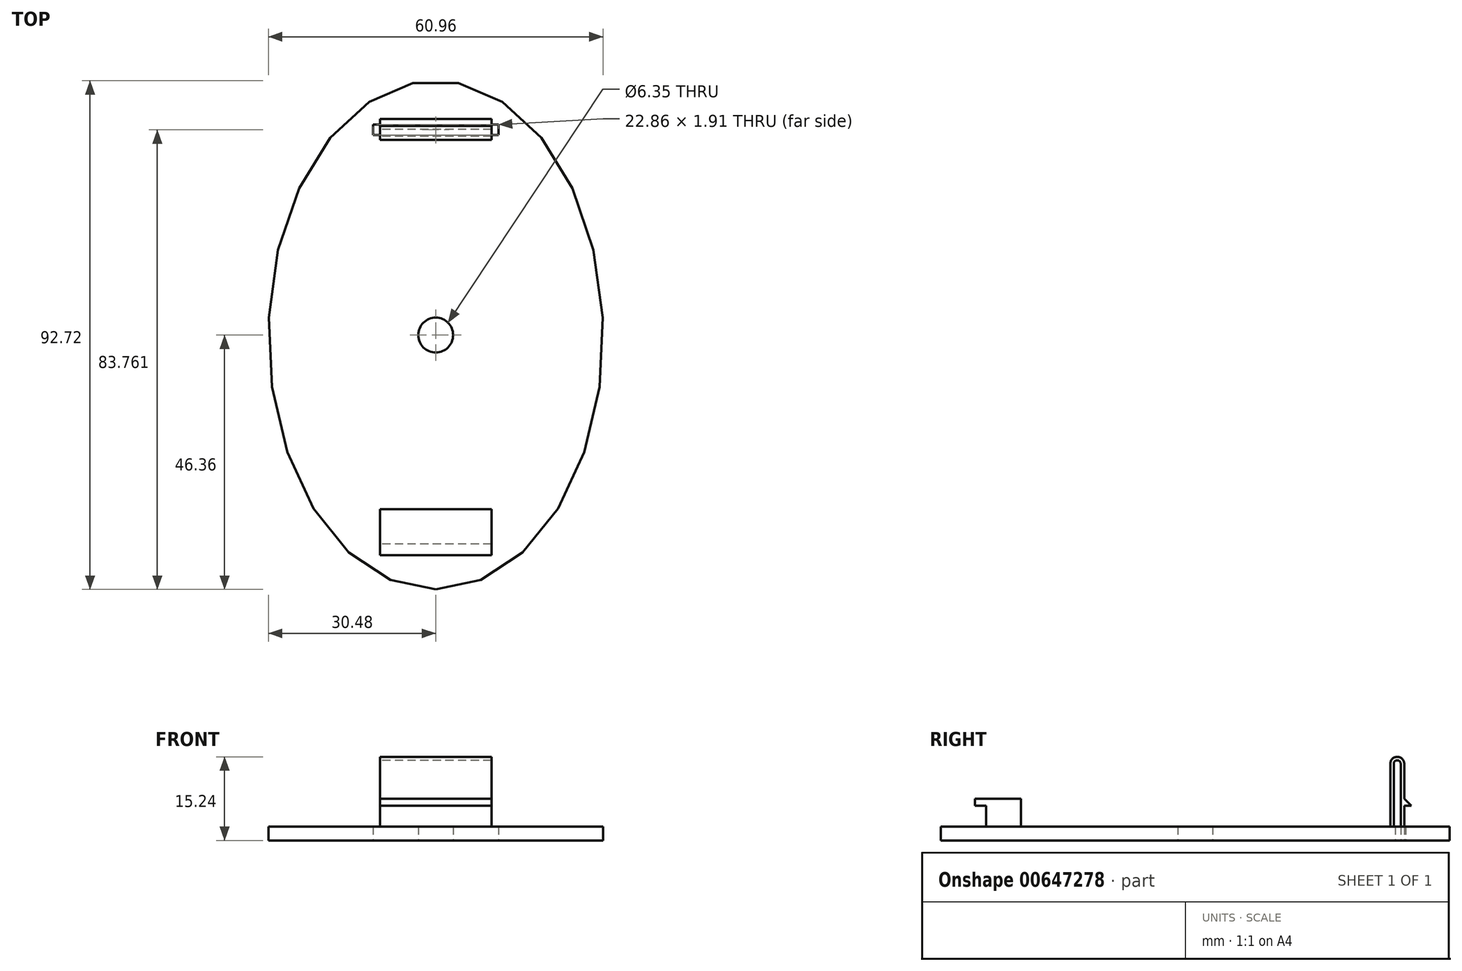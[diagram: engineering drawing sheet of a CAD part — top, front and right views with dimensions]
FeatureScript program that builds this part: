
annotation { "Feature Type Name" : "Feature", "Feature Type Description" : "" }
export const myFeature = defineFeature(function(context is Context, id is Id, definition is map)
    precondition{}
    {
        {
            var Q0;
            Q0=qCreatedBy(makeId("Top.planeOp"),FACE);
            var sketch = newSketch(context, id + "F0", { "sketchPlane" : qUnion([Q0])});
            skEllipse(sketch, "E0", {"center": v(0, 0) * mm, "majorRadius": 46.35 * mm, "minorRadius": 30.48 * mm, "majorAxis": v(0, -1)});
            skCircle(sketch, "E1", {"center": v(0, 0) * mm, "radius": 3.18 * mm});
            skPoint(sketch, "E2.endSnap0", {"position": v(0, 46.35) * mm});
            skSolve(sketch);
        }
        {
            var Q0;
            Q0=makeQuery(id+"F0.imprint","IMPRINT",FACE,{"disambiguationData":[TD([[makeQuery(id+"F0.imprint","IMPRINT",EDGE,{"derivedFrom":sQuery(id+"F0.wireOp",EDGE,"E0")}),1.0]])]});
            extrude(context, id + "F1", {"entities" : qUnion([Q0]), "depth" : 2.54 * mm, "offsetDistance" : 25.4 * mm});
        }
        {
            var Q0;
            Q0=makeQuery(id+"F1.opExtrude","CAP_FACE",FACE,{"disambiguationData":[OSD([sQuery(id+"F0.wireOp",EDGE,"E0"),sQuery(id+"F0.wireOp",EDGE,"E1")])],"isStart":false});
            var sketch = newSketch(context, id + "F2", { "sketchPlane" : qUnion([Q0])});
            skLineSegment(sketch, "E3", {"start": v(0, 0) * mm, "end": v(0, 38.1) * mm, "construction": true});
            skPoint(sketch, "E3.endSnap0", {"position": v(0, 46.35) * mm});
            skLineSegment(sketch, "E4", {"start": v(0, 0) * mm, "end": v(0, -38.1) * mm, "construction": true});
            skLineSegment(sketch, "E5", {"start": v(0, 38.1) * mm, "end": v(10.16, 38.1) * mm});
            skLineSegment(sketch, "E6", {"start": v(0, 38.1) * mm, "end": v(-10.16, 38.1) * mm});
            skLineSegment(sketch, "E7", {"start": v(-10.16, 38.1) * mm, "end": v(-10.16, 31.75) * mm});
            skLineSegment(sketch, "E8", {"start": v(-10.16, 31.75) * mm, "end": v(10.16, 31.75) * mm});
            skLineSegment(sketch, "E9", {"start": v(10.16, 31.75) * mm, "end": v(10.16, 38.1) * mm});
            skLineSegment(sketch, "E10", {"start": v(0, 0) * mm, "end": v(30.48, 0) * mm, "construction": true});
            skLineSegment(sketch, "E11.MirrorCS", {"start": v(-10.16, -31.75) * mm, "end": v(10.16, -31.75) * mm});
            skLineSegment(sketch, "E12.MirrorCS", {"start": v(-10.16, -38.1) * mm, "end": v(-10.16, -31.75) * mm});
            skLineSegment(sketch, "E13.MirrorCS", {"start": v(0, -38.1) * mm, "end": v(-10.16, -38.1) * mm});
            skLineSegment(sketch, "E14.MirrorCS", {"start": v(0, -38.1) * mm, "end": v(10.16, -38.1) * mm});
            skLineSegment(sketch, "E15.MirrorCS", {"start": v(10.16, -31.75) * mm, "end": v(10.16, -38.1) * mm});
            skSolve(sketch);
        }
        {
            var Q0;
            Q0=makeQuery(id+"F2.imprint","IMPRINT",FACE,{"disambiguationData":[TD([[makeQuery(id+"F2.imprint","IMPRINT",EDGE,{"derivedFrom":sQuery(id+"F2.wireOp",EDGE,"E11.MirrorCS")}),-1.0]])]});
            extrude(context, id + "F3", {"entities" : qUnion([Q0]), "operationType" : NewBodyOperationType.ADD, "depth" : 5.08 * mm, "offsetDistance" : 25.4 * mm});
        }
        {
            var Q0;
            Q0=makeQuery(id+"F3.opExtrude","SWEPT_FACE",FACE,{"disambiguationData":[OSD([sQuery(id+"F2.wireOp",EDGE,"E13.MirrorCS"),sQuery(id+"F2.wireOp",EDGE,"E14.MirrorCS")])]});
            var sketch = newSketch(context, id + "F4", { "sketchPlane" : qUnion([Q0])});
            skLineSegment(sketch, "E16.bottom", {"start": v(-10.16, 7.62) * mm, "end": v(10.16, 7.62) * mm});
            skLineSegment(sketch, "E16.top", {"start": v(-10.16, 6.35) * mm, "end": v(10.16, 6.35) * mm});
            skLineSegment(sketch, "E16.left", {"start": v(-10.16, 7.62) * mm, "end": v(-10.16, 6.35) * mm});
            skLineSegment(sketch, "E16.right", {"start": v(10.16, 7.62) * mm, "end": v(10.16, 6.35) * mm});
            skSolve(sketch);
        }
        {
            var Q0;
            Q0=makeQuery(id+"F4.imprint","IMPRINT",FACE,{"disambiguationData":[TD([[makeQuery(id+"F4.imprint","IMPRINT",EDGE,{"derivedFrom":sQuery(id+"F4.wireOp",EDGE,"E16.bottom")}),1.0]])]});
            extrude(context, id + "F5", {"entities" : qUnion([Q0]), "operationType" : NewBodyOperationType.ADD, "depth" : 2.03 * mm, "offsetDistance" : 25.4 * mm});
        }
        {
            var Q0;
            Q0=qCreatedBy(makeId("Right.planeOp"),FACE);
            var sketch = newSketch(context, id + "F6", { "sketchPlane" : qUnion([Q0])});
            skPoint(sketch, "E17.0", {"position": v(38.1, 2.54) * mm});
            skPoint(sketch, "E18.0", {"position": v(37.46, 2.54) * mm});
            skPoint(sketch, "E19.0", {"position": v(36.2, 2.54) * mm});
            skLineSegment(sketch, "E20.0", {"start": v(38.35, 0) * mm, "end": v(36.45, 0) * mm});
            skLineSegment(sketch, "E21", {"start": v(36.2, 2.54) * mm, "end": v(36.45, 2.54) * mm, "construction": true});
            skLineSegment(sketch, "E22", {"start": v(36.45, 2.54) * mm, "end": v(36.45, 0) * mm});
            skLineSegment(sketch, "E23", {"start": v(38.1, 2.54) * mm, "end": v(38.35, 2.54) * mm, "construction": true});
            skLineSegment(sketch, "E24", {"start": v(38.35, 2.54) * mm, "end": v(38.35, 0) * mm});
            skLineSegment(sketch, "E25", {"start": v(36.45, 2.54) * mm, "end": v(38.35, 2.54) * mm});
            skPoint(sketch, "E26.orphan", {"position": v(46.35, 0) * mm});
            skPoint(sketch, "E27.orphan", {"position": v(-46.35, 0) * mm});
            skSolve(sketch);
        }
        {
            var Q0;
            Q0=makeQuery(id+"F6.imprint","IMPRINT",FACE,{"disambiguationData":[TD([[makeQuery(id+"F6.imprint","IMPRINT",EDGE,{"derivedFrom":sQuery(id+"F6.wireOp",EDGE,"E20.0")}),-1.0]])]});
            extrude(context, id + "F7", {"entities" : qUnion([Q0]), "operationType" : NewBodyOperationType.REMOVE, "oppositeDirection" : true, "depth" : 22.86 * mm, "offsetDistance" : 25.4 * mm, "symmetric" : true});
        }
        {
            var Q0;
            Q0=qCreatedBy(makeId("Right.planeOp"),FACE);
            var sketch = newSketch(context, id + "F8", { "sketchPlane" : qUnion([Q0])});
            skLineSegment(sketch, "E28.0", {"start": v(46.35, 2.54) * mm, "end": v(-46.35, 2.54) * mm});
            skPoint(sketch, "E29.0", {"position": v(0, 0) * mm});
            skLineSegment(sketch, "E30", {"start": v(0, 2.54) * mm, "end": v(38.1, 2.54) * mm, "construction": true});
            skLineSegment(sketch, "E31", {"start": v(38.1, 2.54) * mm, "end": v(35.56, 2.54) * mm, "construction": true});
            skLineSegment(sketch, "E32", {"start": v(35.56, 2.54) * mm, "end": v(35.56, 13.97) * mm});
            skLineSegment(sketch, "E33", {"start": v(35.56, 13.97) * mm, "end": v(38.1, 13.97) * mm, "construction": true});
            skArc(sketch, "E34", {"start": v(35.56, 13.97) * mm, "mid": v(36.83, 15.24) * mm, "end": v(38.1, 13.97) * mm});
            skLineSegment(sketch, "E35", {"start": v(38.1, 13.97) * mm, "end": v(38.1, 0) * mm});
            skLineSegment(sketch, "E36.0", {"start": v(37.46, 13.97) * mm, "end": v(37.46, 0) * mm});
            skArc(sketch, "E36.1", {"start": v(36.2, 13.97) * mm, "mid": v(36.83, 14.6) * mm, "end": v(37.46, 13.97) * mm});
            skLineSegment(sketch, "E36.2", {"start": v(36.2, 2.54) * mm, "end": v(36.2, 13.97) * mm});
            skLineSegment(sketch, "E37", {"start": v(37.46, 0) * mm, "end": v(38.1, 0) * mm});
            skLineSegment(sketch, "E38", {"start": v(38.1, 13.97) * mm, "end": v(38.1, 6.35) * mm, "construction": true});
            skLineSegment(sketch, "E39", {"start": v(38.1, 6.35) * mm, "end": v(39.37, 6.35) * mm});
            skLineSegment(sketch, "E40", {"start": v(39.37, 6.35) * mm, "end": v(38.1, 7.62) * mm});
            skSolve(sketch);
        }
        {
            var Q0;
            {var subQ1=sQuery(id+"F8.wireOp",EDGE,"E32");Q0=makeQuery(id+"F8.imprint","IMPRINT",FACE,{"disambiguationData":[TD([[makeQuery(id+"F8.imprint","IMPRINT",EDGE,{"derivedFrom":subQ1}),-1.0]])]});}
            var Q1;
            {var subQ0=sQuery(id+"F8.wireOp",EDGE,"E39");Q1=makeQuery(id+"F8.imprint","IMPRINT",FACE,{"disambiguationData":[TD([[makeQuery(id+"F8.imprint","IMPRINT",EDGE,{"derivedFrom":subQ0}),1.0]])]});}
            var Q2;
            {var subQ5=sQuery(id+"F8.wireOp",EDGE,"E37");Q2=makeQuery(id+"F8.imprint","IMPRINT",FACE,{"disambiguationData":[TD([[makeQuery(id+"F8.imprint","IMPRINT",EDGE,{"derivedFrom":subQ5}),1.0]])]});}
            extrude(context, id + "F9", {"entities" : qUnion([Q0, Q1, Q2]), "operationType" : NewBodyOperationType.ADD, "depth" : 20.32 * mm, "offsetDistance" : 25.4 * mm, "symmetric" : true});
        }
    });
